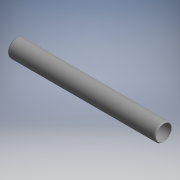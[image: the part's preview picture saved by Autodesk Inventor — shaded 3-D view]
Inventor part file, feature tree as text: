
AUTODESK INVENTOR PART (.ipt)
format: ipt  version: 2017.3 (Build 213256000, 256)  size: 139,264 bytes
history: native  units: mm (DEFAULTED — no unit token found)
features: other x42, sketch x2, revolve x1, extrude x1
ambient origin geometry x8: Origin, YZ Plane, XZ Plane, XY Plane, X Axis, Y Axis, Z Axis, Center Point
bodies: Solid1 (feature_tree)
feature tree (46):
  revolve  "Revolution1"  [1 undecoded]
  extrude  "Extrusion1"  [1 undecoded]
  other  "cp1_XY"
  other  "cp1_YZ"
  other  "cp1_ZX"
  other  "cp1_X"
  other  "cp1_Y"
  other  "cp1_Z"
  other  "cp1_Center"
  other  "cp2_XY"
  other  "cp2_YZ"
  other  "cp2_ZX"
  other  "cp2_X"
  other  "cp2_Y"
  other  "cp2_Z"
  other  "cp2_Center"
  other  "cp3_XY"
  other  "cp3_YZ"
  other  "cp3_ZX"
  other  "cp3_X"
  other  "cp3_Y"
  other  "cp3_Z"
  other  "cp3_Center"
  other  "cp4_XY"
  other  "cp4_YZ"
  other  "cp4_ZX"
  other  "cp4_X"
  other  "cp4_Y"
  other  "cp4_Z"
  other  "cp4_Center"
  other  "tube_front_XY"
  other  "tube_front_YZ"
  other  "tube_front_ZX"
  other  "tube_front_X"
  other  "tube_front_Y"
  other  "tube_front_Z"
  other  "tube_front_Center"
  other  "tube_rear_XY"
  other  "tube_rear_YZ"
  other  "tube_rear_ZX"
  other  "tube_rear_X"
  other  "tube_rear_Y"
  other  "tube_rear_Z"
  other  "tube_rear_Center"
  sketch  "Sketch_1"  dims[d0=360.0deg d1=10.25525mm d2=0.0mm]
  sketch  "Sketch_7"
note: 2 required parameter values undecoded (feature->parameter linkage not recoverable at this tier; creation-order binding heuristic only, values carry confidence <= 0.55)